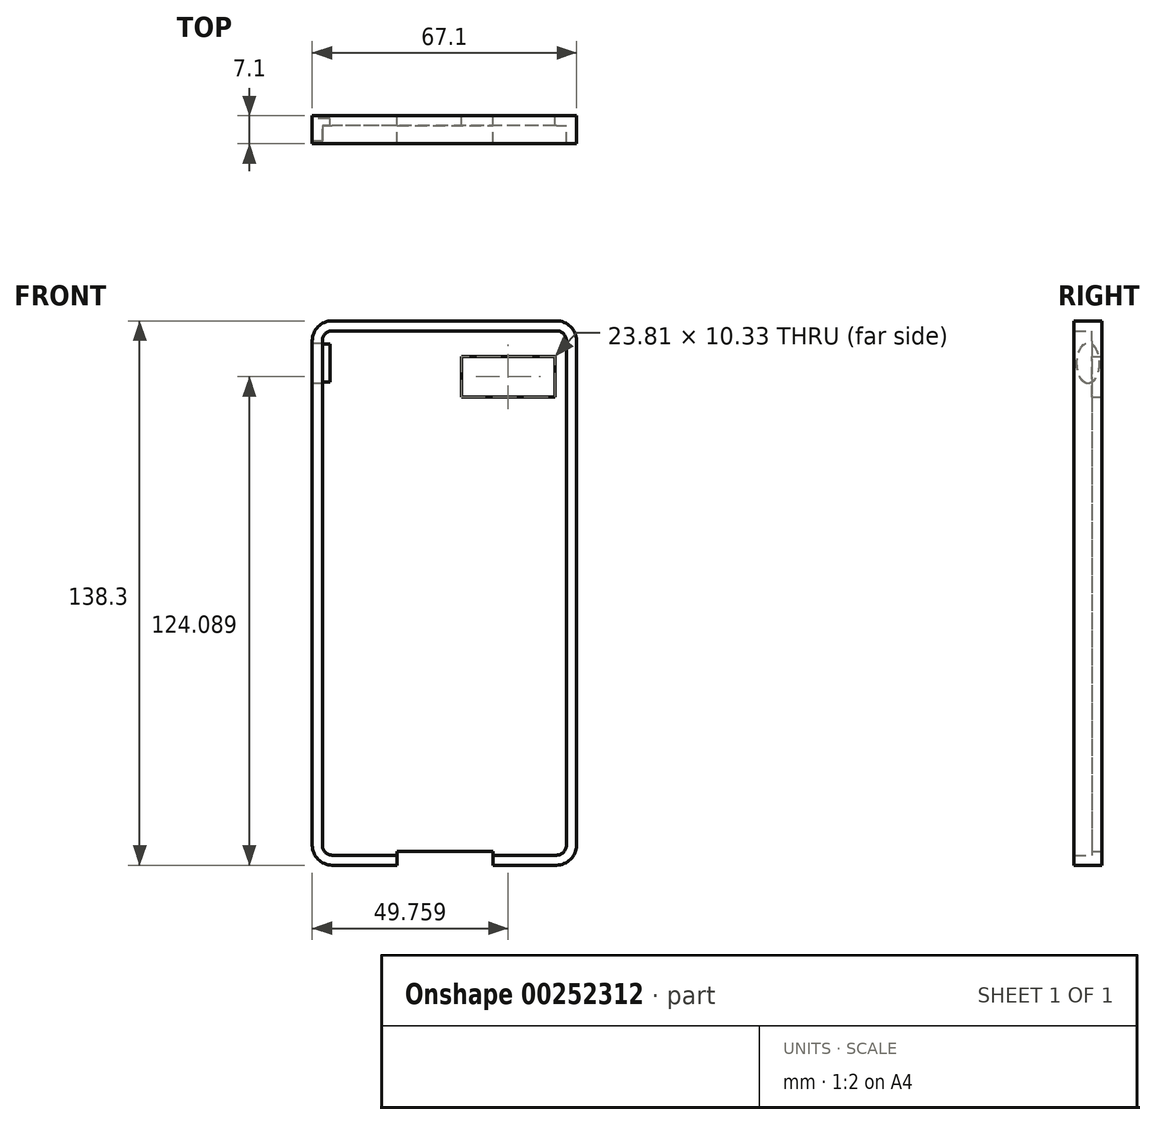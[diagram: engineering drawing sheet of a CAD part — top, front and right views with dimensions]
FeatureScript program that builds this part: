
annotation { "Feature Type Name" : "Feature", "Feature Type Description" : "" }
export const myFeature = defineFeature(function(context is Context, id is Id, definition is map)
    precondition{}
    {
        {
            var Q0;
            Q0=qCreatedBy(makeId("Front.planeOp"),FACE);
            var sketch = newSketch(context, id + "F0", { "sketchPlane" : qUnion([Q0])});
            skLineSegment(sketch, "E0.bottom", {"start": v(33.55, 69.15) * mm, "end": v(-33.55, 69.15) * mm});
            skLineSegment(sketch, "E0.top", {"start": v(33.55, -69.15) * mm, "end": v(-33.55, -69.15) * mm});
            skLineSegment(sketch, "E0.left", {"start": v(33.55, 69.15) * mm, "end": v(33.55, -69.15) * mm});
            skLineSegment(sketch, "E0.right", {"start": v(-33.55, 69.15) * mm, "end": v(-33.55, -69.15) * mm});
            skPoint(sketch, "E0.middle", {"position": v(0, 0) * mm});
            skSolve(sketch);
        }
        {
            var Q0;
            Q0=makeQuery(id+"F0.imprint","IMPRINT",FACE,{"disambiguationData":[TD([[makeQuery(id+"F0.imprint","IMPRINT",EDGE,{"derivedFrom":sQuery(id+"F0.wireOp",EDGE,"E0.bottom")}),1.0]])]});
            extrude(context, id + "F1", {"entities" : qUnion([Q0]), "endBound" : BoundingType.SYMMETRIC, "depth" : 7.1 * mm});
        }
        {
            var Q0;
            Q0=makeQuery(id+"F1.opExtrude","SWEPT_EDGE",EDGE,{"disambiguationData":[OSD([sQuery(id+"F0.wireOp",EDGE,"E0.bottom"),sQuery(id+"F0.wireOp",EDGE,"E0.right")])]});
            var Q1;
            Q1=makeQuery(id+"F1.opExtrude","SWEPT_EDGE",EDGE,{"disambiguationData":[OSD([sQuery(id+"F0.wireOp",EDGE,"E0.bottom"),sQuery(id+"F0.wireOp",EDGE,"E0.left")])]});
            var Q2;
            Q2=makeQuery(id+"F1.opExtrude","SWEPT_EDGE",EDGE,{"disambiguationData":[OSD([sQuery(id+"F0.wireOp",EDGE,"E0.top"),sQuery(id+"F0.wireOp",EDGE,"E0.left")])]});
            var Q3;
            Q3=makeQuery(id+"F1.opExtrude","SWEPT_EDGE",EDGE,{"disambiguationData":[OSD([sQuery(id+"F0.wireOp",EDGE,"E0.top"),sQuery(id+"F0.wireOp",EDGE,"E0.right")])]});
            fillet(context, id + "F2", {"entities" : qUnion([Q0, Q1, Q2, Q3]), "radius" : 5.08 * mm, "tangentPropagation" : true, "allowEdgeOverflow" : false});
        }
        {
            var Q0;
            Q0=makeQuery(id+"F1.opExtrude","CAP_FACE",FACE,{"disambiguationData":[OSD([sQuery(id+"F0.wireOp",EDGE,"E0.bottom"),sQuery(id+"F0.wireOp",EDGE,"E0.top"),sQuery(id+"F0.wireOp",EDGE,"E0.left"),sQuery(id+"F0.wireOp",EDGE,"E0.right")])],"isStart":false});
            shell(context, id + "F3", {"entities" : qUnion([Q0]), "thickness" : 2.54 * mm});
        }
        {
            var Q0;
            Q0=qCreatedBy(makeId("Front.planeOp"),FACE);
            var sketch = newSketch(context, id + "F4", { "sketchPlane" : qUnion([Q0])});
            skLineSegment(sketch, "E1.bottom", {"start": v(4.3, 60.1) * mm, "end": v(28.11, 60.1) * mm});
            skLineSegment(sketch, "E1.top", {"start": v(4.3, 49.77) * mm, "end": v(28.11, 49.77) * mm});
            skLineSegment(sketch, "E1.left", {"start": v(4.3, 60.1) * mm, "end": v(4.3, 49.77) * mm});
            skLineSegment(sketch, "E1.right", {"start": v(28.11, 60.1) * mm, "end": v(28.11, 49.77) * mm});
            skSolve(sketch);
        }
        {
            var Q0;
            Q0 = qSketchRegion(id + "F4", true);
            extrude(context, id + "F5", {"entities" : qUnion([Q0]), "operationType" : NewBodyOperationType.REMOVE, "endBound" : BoundingType.SYMMETRIC, "depth" : 25 * mm});
        }
        {
            var Q0;
            Q0=makeQuery(id+"F1.opExtrude","SWEPT_FACE",FACE,{"disambiguationData":[OSD([sQuery(id+"F0.wireOp",EDGE,"E0.top")])]});
            var sketch = newSketch(context, id + "F6", { "sketchPlane" : qUnion([Q0])});
            skLineSegment(sketch, "E2.bottom", {"start": v(-12.05, 3.55) * mm, "end": v(12.34, 3.55) * mm});
            skLineSegment(sketch, "E2.top", {"start": v(-12.05, -3.55) * mm, "end": v(12.34, -3.55) * mm});
            skLineSegment(sketch, "E2.left", {"start": v(-12.05, 3.55) * mm, "end": v(-12.05, -3.55) * mm});
            skLineSegment(sketch, "E2.right", {"start": v(12.34, 3.55) * mm, "end": v(12.34, -3.55) * mm});
            skSolve(sketch);
        }
        {
            var Q0;
            Q0 = qSketchRegion(id + "F6", true);
            extrude(context, id + "F7", {"entities" : qUnion([Q0]), "operationType" : NewBodyOperationType.REMOVE, "endBound" : BoundingType.SYMMETRIC, "oppositeDirection" : true, "depth" : 7 * mm});
        }
        {
            var Q0;
            Q0=makeQuery(id+"F1.opExtrude","SWEPT_FACE",FACE,{"disambiguationData":[OSD([sQuery(id+"F0.wireOp",EDGE,"E0.right")])]});
            var sketch = newSketch(context, id + "F8", { "sketchPlane" : qUnion([Q0])});
            skEllipse(sketch, "E3", {"center": v(0, 58.38) * mm, "majorRadius": 5.16 * mm, "minorRadius": 2.8 * mm, "majorAxis": v(0, -1)});
            skSolve(sketch);
        }
        {
            var Q0;
            Q0 = qSketchRegion(id + "F8", true);
            extrude(context, id + "F9", {"entities" : qUnion([Q0]), "operationType" : NewBodyOperationType.REMOVE, "endBound" : BoundingType.SYMMETRIC, "oppositeDirection" : true, "depth" : 9 * mm});
        }
    });
